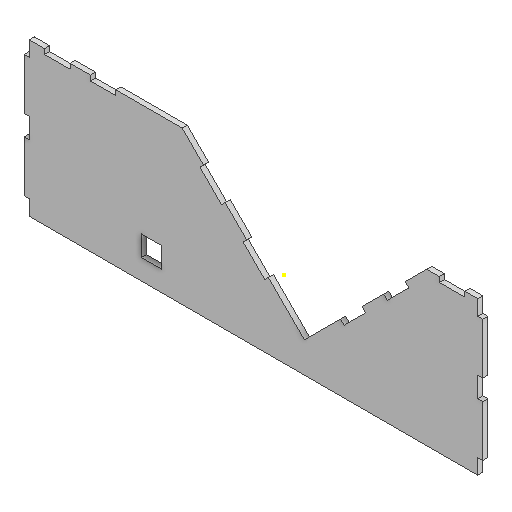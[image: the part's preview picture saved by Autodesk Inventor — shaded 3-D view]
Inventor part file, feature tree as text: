
AUTODESK INVENTOR PART (.ipt)
format: ipt  version: 2022 (Build 260153000, 153)  size: 200,704 bytes
history: native  units: mm
features: reference x5, other x5, sketch x3, extrude x2, projected_geometry x1
ambient origin geometry x8: Origin, YZ Plane, XZ Plane, XY Plane, X Axis, Y Axis, Z Axis, Center Point
bodies: Solid1 (feature_tree)
feature tree (16):
  extrude  "Extrusion1"  Depth=20.0mm
  sketch  "Sketch2"  dims[d5=20.0mm d6=20.0mm]
  extrude  "Extrusion3"  Depth=20.0mm
  sketch  "Sketch1"  dims[d0=5.0mm d1=0.0mm d4=20.0mm]
  reference  "Reference1"
  reference  "Reference2"
  reference  "Reference3"
  reference  "Reference4"
  reference  "Reference5"
  sketch  "Sketch4"  dims[d7=110.0mm d8=10.0mm d9=0.0mm]
  projected_geometry  "Projected Loop2"
  parser-record x1  (decoder bookkeeping rows leaked as tree rows — omitted from the tree; the rows remain in map.json)
  other  "Ensamble caja.iam"
  other  "Modelo base:1"
  other  "Lateral:2"
  other  "Lateral:1"
note: 1 file-system path scrubbed to <path> (originals preserved in map.json)
